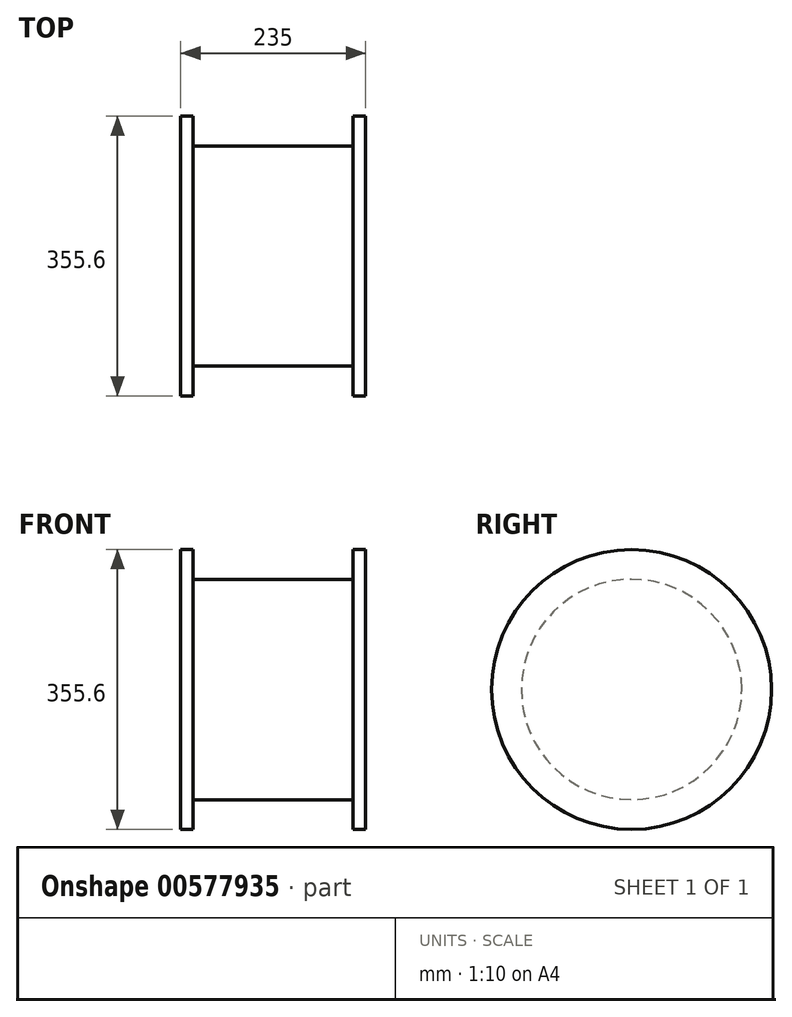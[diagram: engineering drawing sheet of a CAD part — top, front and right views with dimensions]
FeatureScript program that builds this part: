
annotation { "Feature Type Name" : "Feature", "Feature Type Description" : "" }
export const myFeature = defineFeature(function(context is Context, id is Id, definition is map)
    precondition{}
    {
        {
            var Q0;
            Q0=qCreatedBy(makeId("Front.planeOp"),FACE);
            var sketch = newSketch(context, id + "F0", { "sketchPlane" : qUnion([Q0])});
            skLineSegment(sketch, "E0", {"start": v(0, 140) * mm, "end": v(101.6, 140) * mm});
            skLineSegment(sketch, "E1", {"start": v(101.6, 140) * mm, "end": v(101.6, 177.8) * mm});
            skLineSegment(sketch, "E2", {"start": v(101.6, 177.8) * mm, "end": v(117.5, 177.8) * mm});
            skLineSegment(sketch, "E3", {"start": v(117.5, 177.8) * mm, "end": v(117.5, 0) * mm});
            skLineSegment(sketch, "E4", {"start": v(0, 0) * mm, "end": v(117.5, 0) * mm});
            skLineSegment(sketch, "E5.MirrorCS", {"start": v(-101.6, 177.8) * mm, "end": v(-117.5, 177.8) * mm});
            skLineSegment(sketch, "E6.MirrorCS", {"start": v(0, 140) * mm, "end": v(-101.6, 140) * mm});
            skLineSegment(sketch, "E7.MirrorCS", {"start": v(0, 0) * mm, "end": v(-117.5, 0) * mm});
            skLineSegment(sketch, "E8.MirrorCS", {"start": v(-101.6, 140) * mm, "end": v(-101.6, 177.8) * mm});
            skLineSegment(sketch, "E9.MirrorCS", {"start": v(-117.5, 177.8) * mm, "end": v(-117.5, 0) * mm});
            skLineSegment(sketch, "E10", {"start": v(-193.98, 0) * mm, "end": v(285.48, 0) * mm, "construction": true});
            skSolve(sketch);
        }
        {
            var Q0;
            Q0=makeQuery(id+"F0.imprint","IMPRINT",FACE,{"disambiguationData":[TD([[makeQuery(id+"F0.imprint","IMPRINT",EDGE,{"derivedFrom":sQuery(id+"F0.wireOp",EDGE,"E0")}),-1.0]])]});
            var Q1;
            Q1=sQuery(id+"F0.wireOp",EDGE,"E10");
            revolve(context, id + "F1", {"surfaceOperationType" : NewSurfaceOperationType.NEW, "entities" : qUnion([Q0]), "axis" : qUnion([Q1]), "revolveType" : RevolveType.FULL});
        }
    });
